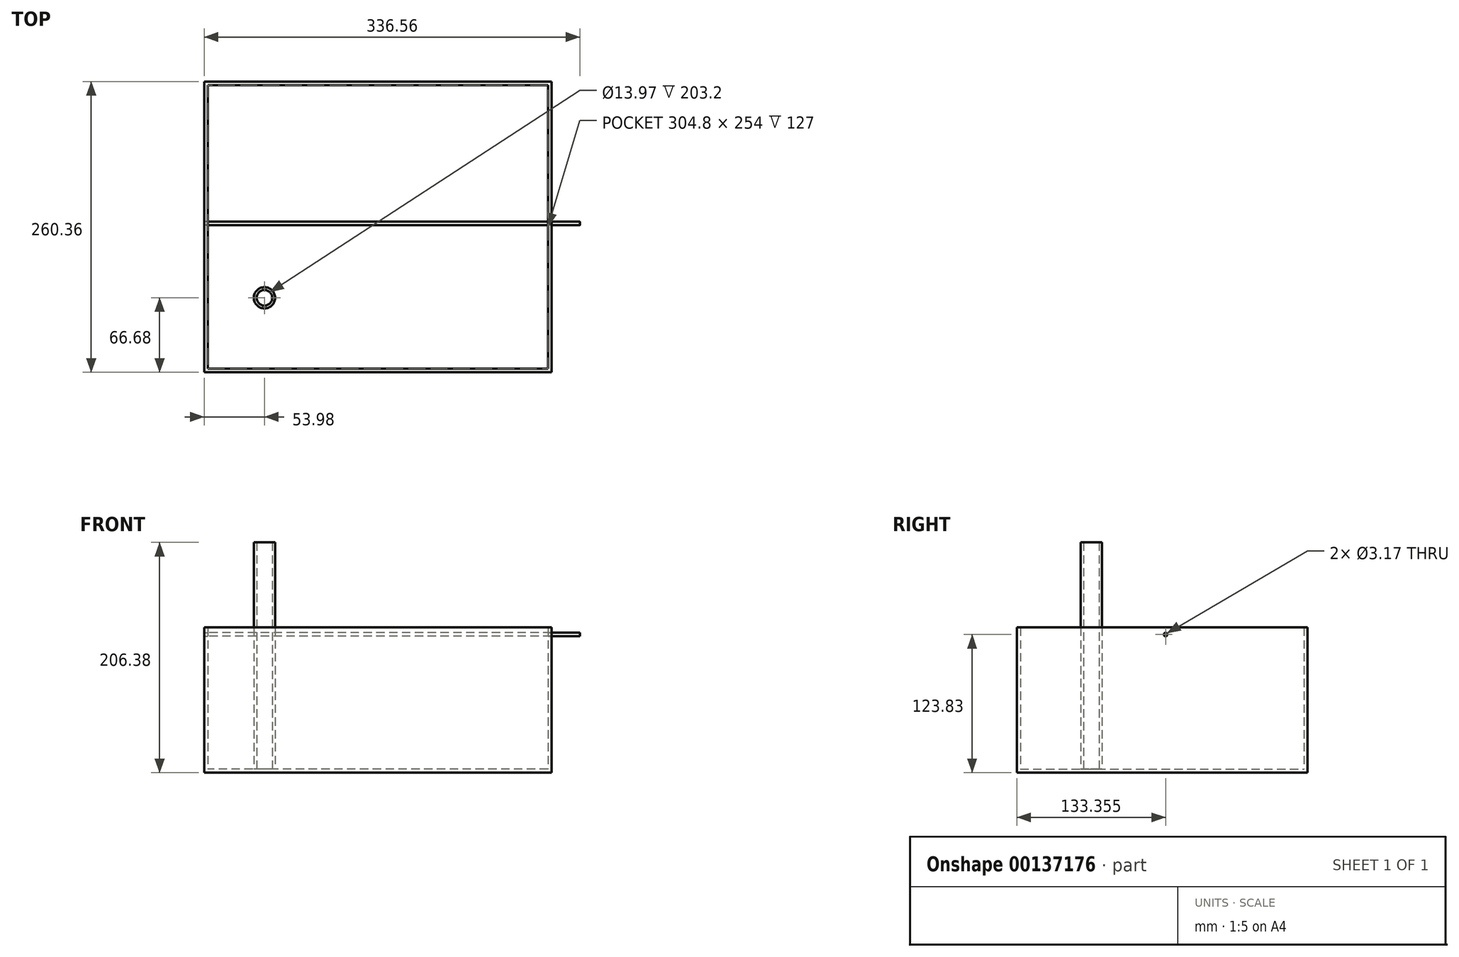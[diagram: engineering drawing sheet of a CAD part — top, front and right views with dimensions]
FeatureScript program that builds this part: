
annotation { "Feature Type Name" : "Feature", "Feature Type Description" : "" }
export const myFeature = defineFeature(function(context is Context, id is Id, definition is map)
    precondition{}
    {
        {
            var Q0;
            Q0=qCreatedBy(makeId("Top.planeOp"),FACE);
            var sketch = newSketch(context, id + "F0", { "sketchPlane" : qUnion([Q0])});
            skLineSegment(sketch, "E0.bottom", {"start": v(152.4, -127) * mm, "end": v(-152.4, -127) * mm});
            skLineSegment(sketch, "E0.top", {"start": v(152.4, 127) * mm, "end": v(-152.4, 127) * mm});
            skLineSegment(sketch, "E0.left", {"start": v(152.4, -127) * mm, "end": v(152.4, 127) * mm});
            skLineSegment(sketch, "E0.right", {"start": v(-152.4, -127) * mm, "end": v(-152.4, 127) * mm});
            skPoint(sketch, "E0.middle", {"position": v(0, 0) * mm});
            skLineSegment(sketch, "E1.0", {"start": v(155.58, 130.17) * mm, "end": v(-155.58, 130.17) * mm});
            skLineSegment(sketch, "E1.1", {"start": v(155.58, -130.18) * mm, "end": v(155.58, 130.17) * mm});
            skLineSegment(sketch, "E1.2", {"start": v(155.58, -130.18) * mm, "end": v(-155.58, -130.18) * mm});
            skLineSegment(sketch, "E1.3", {"start": v(-155.58, -130.18) * mm, "end": v(-155.58, 130.17) * mm});
            skSolve(sketch);
        }
        {
            var Q0;
            Q0=qSketchRegion(id+"F0",true);
            extrude(context, id + "F1", {"entities" : qUnion([Q0]), "depth" : 127 * mm});
        }
        {
            var Q0;
            Q0=makeQuery(id+"F1.opExtrude","CAP_FACE",FACE,{"disambiguationData":[OSD([sQuery(id+"F0.wireOp",EDGE,"E0.bottom"),sQuery(id+"F0.wireOp",EDGE,"E0.top"),sQuery(id+"F0.wireOp",EDGE,"E0.left"),sQuery(id+"F0.wireOp",EDGE,"E0.right"),sQuery(id+"F0.wireOp",EDGE,"E1.0"),sQuery(id+"F0.wireOp",EDGE,"E1.1"),sQuery(id+"F0.wireOp",EDGE,"E1.2"),sQuery(id+"F0.wireOp",EDGE,"E1.3")])],"isStart":true});
            var sketch = newSketch(context, id + "F2", { "sketchPlane" : qUnion([Q0])});
            skLineSegment(sketch, "E2.0", {"start": v(-155.58, 130.18) * mm, "end": v(-155.58, -130.17) * mm});
            skLineSegment(sketch, "E3.0", {"start": v(155.58, -130.17) * mm, "end": v(-155.58, -130.17) * mm});
            skLineSegment(sketch, "E4.0", {"start": v(155.58, 130.18) * mm, "end": v(155.58, -130.17) * mm});
            skLineSegment(sketch, "E5.0", {"start": v(155.58, 130.18) * mm, "end": v(-155.58, 130.18) * mm});
            skSolve(sketch);
        }
        {
            var Q0;
            Q0=qSketchRegion(id+"F2",true);
            extrude(context, id + "F3", {"entities" : qUnion([Q0]), "operationType" : NewBodyOperationType.ADD, "depth" : 3.17 * mm});
        }
        {
            var Q0;
            Q0=makeQuery(id+"F3.opExtrude","CAP_FACE",FACE,{"disambiguationData":[OSD([sQuery(id+"F2.wireOp",EDGE,"E2.0"),sQuery(id+"F2.wireOp",EDGE,"E3.0"),sQuery(id+"F2.wireOp",EDGE,"E4.0"),sQuery(id+"F2.wireOp",EDGE,"E5.0")])],"isStart":true});
            var sketch = newSketch(context, id + "F4", { "sketchPlane" : qUnion([Q0])});
            skLineSegment(sketch, "E6.bottom", {"start": v(-139.7, -114.3) * mm, "end": v(-38.1, -114.3) * mm, "construction": true});
            skLineSegment(sketch, "E6.top", {"start": v(-139.7, -12.7) * mm, "end": v(-38.1, -12.7) * mm, "construction": true});
            skLineSegment(sketch, "E6.left", {"start": v(-139.7, -114.3) * mm, "end": v(-139.7, -12.7) * mm, "construction": true});
            skLineSegment(sketch, "E6.right", {"start": v(-38.1, -114.3) * mm, "end": v(-38.1, -12.7) * mm, "construction": true});
            skCircle(sketch, "E7", {"center": v(-139.7, -114.3) * mm, "radius": 1.27 * mm});
            skCircle(sketch, "E8", {"center": v(-38.1, -114.3) * mm, "radius": 1.27 * mm});
            skCircle(sketch, "E9", {"center": v(-139.7, -12.7) * mm, "radius": 1.27 * mm});
            skCircle(sketch, "E10", {"center": v(-38.1, -12.7) * mm, "radius": 1.27 * mm});
            skLineSegment(sketch, "E11", {"start": v(-139.7, -114.3) * mm, "end": v(-38.1, -12.7) * mm, "construction": true});
            skLineSegment(sketch, "E12", {"start": v(-139.7, -63.5) * mm, "end": v(-38.1, -63.5) * mm, "construction": true});
            skCircle(sketch, "E13", {"center": v(-101.6, -63.5) * mm, "radius": 9.53 * mm});
            skCircle(sketch, "E14", {"center": v(-50.8, -63.5) * mm, "radius": 15.88 * mm});
            skCircle(sketch, "E15", {"center": v(-50.8, -63.5) * mm, "radius": 28.58 * mm, "construction": true});
            skCircle(sketch, "E16", {"center": v(-101.6, -63.5) * mm, "radius": 6.99 * mm});
            skCircle(sketch, "E17", {"center": v(-50.8, -63.5) * mm, "radius": 13.33 * mm});
            skSolve(sketch);
        }
        {
            var Q0;
            Q0=makeQuery(id+"F3.boolean.opBoolean","MERGE",FACE,{"derivedFrom":[makeQuery(id+"F1.opExtrude","SWEPT_FACE",FACE,{"disambiguationData":[OSD([sQuery(id+"F0.wireOp",EDGE,"E1.1")])]}),makeQuery(id+"F3.opExtrude","SWEPT_FACE",FACE,{"disambiguationData":[OSD([sQuery(id+"F2.wireOp",EDGE,"E4.0")])]})]});
            var sketch = newSketch(context, id + "F5", { "sketchPlane" : qUnion([Q0])});
            skCircle(sketch, "E18", {"center": v(3.17, 120.65) * mm, "radius": 1.59 * mm});
            skSolve(sketch);
        }
        {
            var Q0;
            Q0=qSketchRegion(id+"F5",true);
            extrude(context, id + "F6", {"entities" : qUnion([Q0]), "operationType" : NewBodyOperationType.REMOVE, "endBound" : BoundingType.THROUGH_ALL, "oppositeDirection" : true, "depth" : 25.4 * mm});
        }
        {
            var Q0;
            Q0=makeQuery(id+"F3.boolean.opBoolean","MERGE",FACE,{"derivedFrom":[makeQuery(id+"F1.opExtrude","SWEPT_FACE",FACE,{"disambiguationData":[OSD([sQuery(id+"F0.wireOp",EDGE,"E1.1")])]}),makeQuery(id+"F3.opExtrude","SWEPT_FACE",FACE,{"disambiguationData":[OSD([sQuery(id+"F2.wireOp",EDGE,"E4.0")])]})]});
            var sketch = newSketch(context, id + "F7", { "sketchPlane" : qUnion([Q0])});
            skCircle(sketch, "E19.0", {"center": v(3.17, 120.65) * mm, "radius": 1.59 * mm});
            skSolve(sketch);
        }
        {
            var Q0;
            Q0=qSketchRegion(id+"F7",true);
            var Q1;
            Q1=makeQuery(id+"F3.boolean.opBoolean","MERGE",FACE,{"derivedFrom":[makeQuery(id+"F1.opExtrude","SWEPT_FACE",FACE,{"disambiguationData":[OSD([sQuery(id+"F0.wireOp",EDGE,"E1.3")])]}),makeQuery(id+"F3.opExtrude","SWEPT_FACE",FACE,{"disambiguationData":[OSD([sQuery(id+"F2.wireOp",EDGE,"E2.0")])]})]});
            extrude(context, id + "F8", {"entities" : qUnion([Q0]), "depth" : 25.4 * mm, "hasSecondDirection" : true, "secondDirectionBound" : SecondDirectionBoundingType.UP_TO_SURFACE, "secondDirectionOppositeDirection" : true, "secondDirectionBoundEntityFace" : qUnion([Q1]), "secondDirectionDepth" : 25.4 * mm});
        }
        {
            var Q0;
            Q0=makeQuery(id+"F4.imprint","IMPRINT",FACE,{"disambiguationData":[TD([[makeQuery(id+"F4.imprint","IMPRINT",EDGE,{"derivedFrom":sQuery(id+"F4.wireOp",EDGE,"E13")}),1.0]])]});
            extrude(context, id + "F9", {"entities" : qUnion([Q0]), "depth" : 203.2 * mm});
        }
    });
